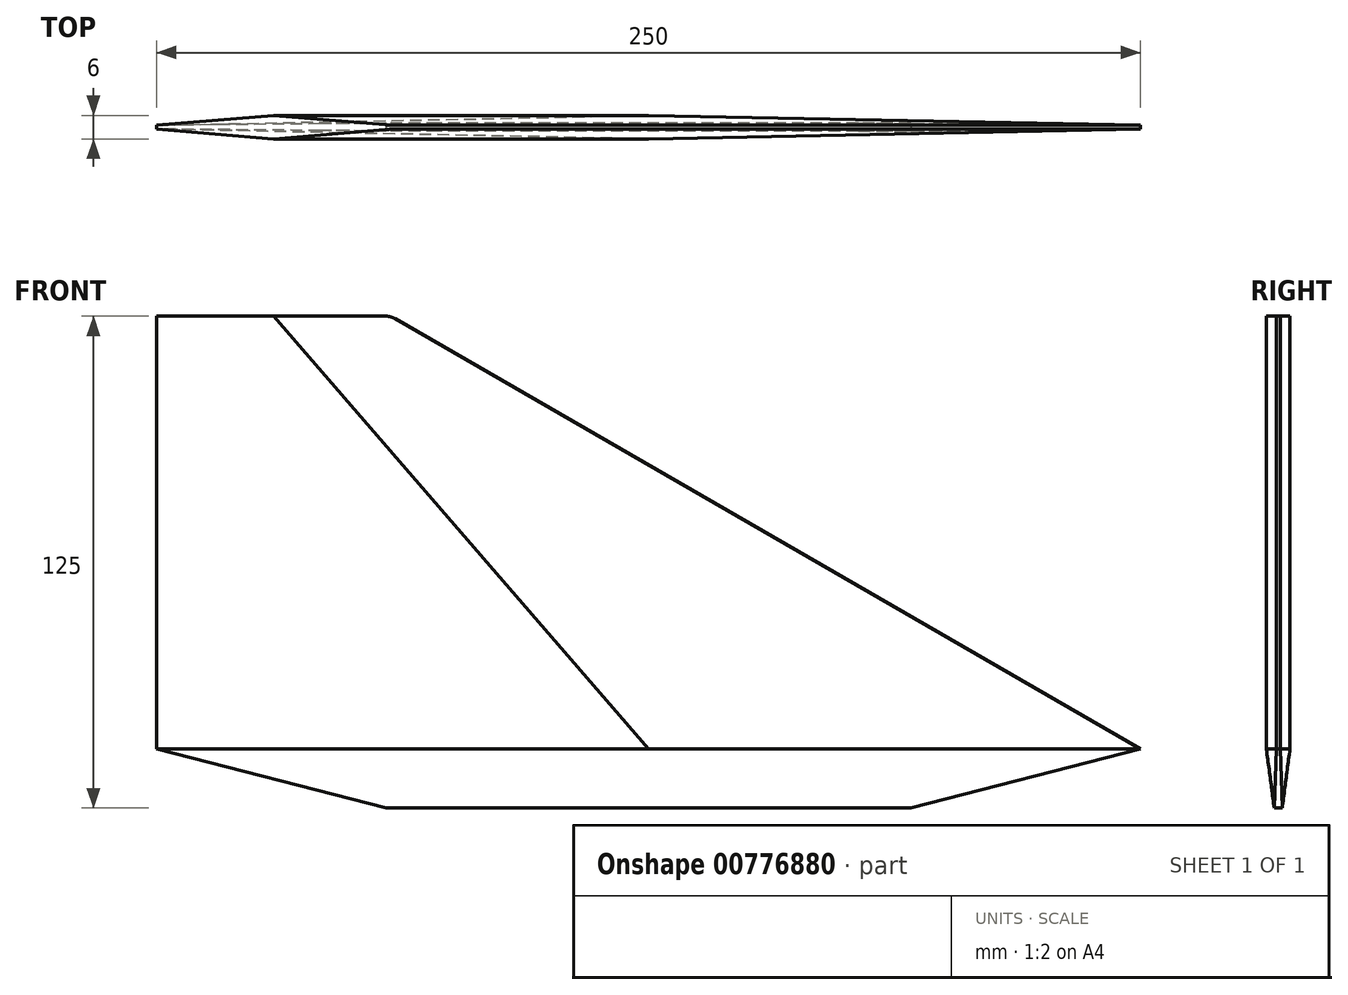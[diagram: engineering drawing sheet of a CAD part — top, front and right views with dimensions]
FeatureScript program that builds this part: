
annotation { "Feature Type Name" : "Feature", "Feature Type Description" : "" }
export const myFeature = defineFeature(function(context is Context, id is Id, definition is map)
    precondition{}
    {
        {
            var Q0;
            Q0=qCreatedBy(makeId("Top.planeOp"),FACE);
            cPlane(context, id + "F0", {"entities" : qUnion([Q0]), "cplaneType" : CPlaneType.OFFSET, "offset" : 15 * mm, "width" : 152.4 * mm, "height" : 152.4 * mm});
        }
        {
            var Q0;
            Q0=qCreatedBy(id+"F0.planeOp",FACE);
            cPlane(context, id + "F1", {"entities" : qUnion([Q0]), "cplaneType" : CPlaneType.OFFSET, "offset" : 110 * mm, "width" : 150 * mm, "height" : 150 * mm});
        }
        {
            var Q0;
            Q0=qCreatedBy(id+"F0.planeOp",FACE);
            var sketch = newSketch(context, id + "F2", { "sketchPlane" : qUnion([Q0])});
            skLineSegment(sketch, "E0", {"start": v(0, -3) * mm, "end": v(0, 0) * mm, "construction": true});
            skLineSegment(sketch, "E1", {"start": v(0, 0) * mm, "end": v(0, 3) * mm, "construction": true});
            skLineSegment(sketch, "E2", {"start": v(0, -3) * mm, "end": v(125, -0.5) * mm});
            skLineSegment(sketch, "E3", {"start": v(125, -0.5) * mm, "end": v(125, 0.5) * mm});
            skLineSegment(sketch, "E4", {"start": v(125, 0.5) * mm, "end": v(0, 3) * mm});
            skLineSegment(sketch, "E5.MirrorCS", {"start": v(-125, -0.5) * mm, "end": v(-125, 0.5) * mm});
            skLineSegment(sketch, "E6.MirrorCS", {"start": v(0, -3) * mm, "end": v(-125, -0.5) * mm});
            skLineSegment(sketch, "E7.MirrorCS", {"start": v(-125, 0.5) * mm, "end": v(0, 3) * mm});
            skSolve(sketch);
        }
        {
            var Q0;
            Q0=qCreatedBy(id+"F1.planeOp",FACE);
            var sketch = newSketch(context, id + "F3", { "sketchPlane" : qUnion([Q0])});
            skLineSegment(sketch, "E8", {"start": v(-95.26, -3) * mm, "end": v(-95.26, 0) * mm, "construction": true});
            skLineSegment(sketch, "E9", {"start": v(-95.26, 0) * mm, "end": v(-95.26, 3) * mm, "construction": true});
            skLineSegment(sketch, "E10", {"start": v(-95.26, -3) * mm, "end": v(-65.53, -0.5) * mm});
            skLineSegment(sketch, "E11", {"start": v(-65.53, -0.5) * mm, "end": v(-65.53, 0.5) * mm});
            skLineSegment(sketch, "E12", {"start": v(-65.53, 0.5) * mm, "end": v(-95.26, 3) * mm});
            skLineSegment(sketch, "E13.MirrorCS", {"start": v(-125, -0.5) * mm, "end": v(-125, 0.5) * mm});
            skLineSegment(sketch, "E14.MirrorCS", {"start": v(-95.26, -3) * mm, "end": v(-125, -0.5) * mm});
            skLineSegment(sketch, "E15.MirrorCS", {"start": v(-125, 0.5) * mm, "end": v(-95.26, 3) * mm});
            skSolve(sketch);
        }
        {
            var Q0;
            Q0=qCreatedBy(makeId("Top.planeOp"),FACE);
            var sketch = newSketch(context, id + "F4", { "sketchPlane" : qUnion([Q0])});
            skLineSegment(sketch, "E16.left", {"start": v(-66.67, 1) * mm, "end": v(-66.67, -1) * mm});
            skLineSegment(sketch, "E16.right", {"start": v(66.67, 1) * mm, "end": v(66.67, -1) * mm});
            skPoint(sketch, "E16.middle", {"position": v(0, 0) * mm});
            skLineSegment(sketch, "E17", {"start": v(66.67, 1) * mm, "end": v(0, 1) * mm});
            skLineSegment(sketch, "E18", {"start": v(0, 1) * mm, "end": v(-66.67, 1) * mm});
            skLineSegment(sketch, "E19", {"start": v(66.67, -1) * mm, "end": v(0, -1) * mm});
            skLineSegment(sketch, "E20", {"start": v(0, -1) * mm, "end": v(-66.67, -1) * mm});
            skSolve(sketch);
        }
        {
            var Q0;
            Q0=qSketchRegion(id+"F4",true);
            var Q1;
            Q1=qSketchRegion(id+"F2",true);
            loft(context, id + "F5", {"sheetProfilesArray" : [{ "sheetProfileEntities" : qUnion([Q0]) }, { "sheetProfileEntities" : qUnion([Q1]) }]});
        }
        {
            var Q1;
            Q1=qSketchRegion(id+"F3",true);
            var Q2;
            Q2=qSketchRegion(id+"F2",true);
            loft(context, id + "F6", {"operationType" : NewBodyOperationType.ADD, "sheetProfilesArray" : [{ "sheetProfileEntities" : qUnion([Q1]) }, { "sheetProfileEntities" : qUnion([Q2]) }]});
        }
        {
            var Q0;
            Q0=qCreatedBy(makeId("Right.planeOp"),FACE);
            cPlane(context, id + "F7", {"entities" : qUnion([Q0]), "cplaneType" : CPlaneType.OFFSET, "offset" : 115 * mm, "oppositeDirection" : true, "width" : 150 * mm, "height" : 150 * mm});
        }
        {
            var Q0;
            Q0=qCreatedBy(makeId("Right.planeOp"),FACE);
            cPlane(context, id + "F8", {"entities" : qUnion([Q0]), "cplaneType" : CPlaneType.OFFSET, "offset" : 125 * mm, "width" : 150 * mm, "height" : 150 * mm});
        }
        {
            var Q0;
            Q0=qCreatedBy(id+"F7.planeOp",FACE);
            var sketch = newSketch(context, id + "F9", { "sketchPlane" : qUnion([Q0])});
            skLineSegment(sketch, "E21", {"start": v(0, 0) * mm, "end": v(0, -93.63) * mm, "construction": true});
            skArc(sketch, "E22", {"start": v(45.5, -22.12) * mm, "mid": v(0, -7) * mm, "end": v(-45.5, -22.12) * mm, "construction": true});
            skArc(sketch, "E23", {"start": v(20, -9.68) * mm, "mid": v(0, -7) * mm, "end": v(-20, -9.68) * mm});
            skLineSegment(sketch, "E24", {"start": v(0.5, 15) * mm, "end": v(-0.5, 15) * mm});
            skArc(sketch, "E25", {"start": v(0.5, 15) * mm, "mid": v(9.76, 2.28) * mm, "end": v(20, -9.68) * mm});
            skArc(sketch, "E26", {"start": v(-20, -9.68) * mm, "mid": v(-9.76, 2.28) * mm, "end": v(-0.5, 15) * mm});
            skSolve(sketch);
        }
        {
            var Q0;
            Q0=qCreatedBy(makeId("Right.planeOp"),FACE);
            var sketch = newSketch(context, id + "F10", { "sketchPlane" : qUnion([Q0])});
            skLineSegment(sketch, "E27", {"start": v(0, -1.91) * mm, "end": v(0, -93.63) * mm, "construction": true});
            skArc(sketch, "E28", {"start": v(45.5, -22.12) * mm, "mid": v(0, -7) * mm, "end": v(-45.5, -22.12) * mm, "construction": true});
            skArc(sketch, "E29", {"start": v(20, -9.68) * mm, "mid": v(0, -7) * mm, "end": v(-20, -9.68) * mm});
            skArc(sketch, "E30", {"start": v(3, 15) * mm, "mid": v(10.33, 1.86) * mm, "end": v(20, -9.68) * mm});
            skArc(sketch, "E31.MirrorCS", {"start": v(-3, 15) * mm, "mid": v(-10.33, 1.86) * mm, "end": v(-20, -9.68) * mm});
            skLineSegment(sketch, "E32", {"start": v(3, 15) * mm, "end": v(-3, 15) * mm});
            skSolve(sketch);
        }
        {
            var Q0;
            Q0=qCreatedBy(id+"F0.planeOp",FACE);
            var Q1;
            Q1=sQuery(id+"F4.wireOp",EDGE,"E18");
            cPlane(context, id + "F11", {"entities" : qUnion([Q0, Q1]), "cplaneType" : CPlaneType.LINE_ANGLE, "offset" : 25 * mm, "angle" : 15 * degree, "width" : 150 * mm, "height" : 150 * mm});
        }
        {
            var Q0;
            Q0=qCreatedBy(id+"F11.planeOp",FACE);
            cPlane(context, id + "F12", {"entities" : qUnion([Q0]), "cplaneType" : CPlaneType.OFFSET, "offset" : 25 * mm, "oppositeDirection" : true, "width" : 150 * mm, "height" : 150 * mm});
        }
        {
            var Q0;
            Q0=qCreatedBy(id+"F12.planeOp",FACE);
            var sketch = newSketch(context, id + "F13", { "sketchPlane" : qUnion([Q0])});
            skCircle(sketch, "E33", {"center": v(-79.78, -8.83) * mm, "radius": 4.48 * mm});
            skCircle(sketch, "E34.1.0.0", {"center": v(-34.78, -8.83) * mm, "radius": 4.48 * mm});
            skCircle(sketch, "E34.2.0.0", {"center": v(10.22, -8.83) * mm, "radius": 4.48 * mm});
            skLineSegment(sketch, "E34.direction1", {"start": v(-79.78, -8.83) * mm, "end": v(-34.78, -8.83) * mm, "construction": true});
            skSolve(sketch);
        }
        {
            var Q0;
            Q0=qCreatedBy(id+"F12.planeOp",FACE);
            var sketch = newSketch(context, id + "F14", { "sketchPlane" : qUnion([Q0])});
            skCircle(sketch, "E35", {"center": v(-79.78, -8.83) * mm, "radius": 2 * mm});
            skCircle(sketch, "E36.1.0.0", {"center": v(-34.78, -8.83) * mm, "radius": 2 * mm});
            skCircle(sketch, "E36.2.0.0", {"center": v(10.22, -8.83) * mm, "radius": 2 * mm});
            skLineSegment(sketch, "E36.direction1", {"start": v(-79.78, -8.83) * mm, "end": v(-34.78, -8.83) * mm, "construction": true});
            skSolve(sketch);
        }
        {
            var Q0;
            Q0=qSketchRegion(id+"F14",true);
            extrude(context, id + "F15", {"entities" : qUnion([Q0]), "operationType" : NewBodyOperationType.REMOVE, "endBound" : BoundingType.THROUGH_ALL, "depth" : 25 * mm, "offsetDistance" : 25 * mm});
        }
        {
            var Q0;
            Q0=qSketchRegion(id+"F13",true);
            extrude(context, id + "F16", {"entities" : qUnion([Q0]), "operationType" : NewBodyOperationType.REMOVE, "depth" : 26 * mm, "offsetDistance" : 25 * mm});
        }
        {
            var Q0;
            Q0=qCreatedBy(id+"F7.planeOp",FACE);
            cPlane(context, id + "F17", {"entities" : qUnion([Q0]), "cplaneType" : CPlaneType.OFFSET, "offset" : 10 * mm, "oppositeDirection" : true, "width" : 150 * mm, "height" : 150 * mm});
        }
        {
            var Q0;
            Q0=qCreatedBy(id+"F17.planeOp",FACE);
            var sketch = newSketch(context, id + "F18", { "sketchPlane" : qUnion([Q0])});
            skLineSegment(sketch, "E37", {"start": v(0, -2.27) * mm, "end": v(0, -93.99) * mm, "construction": true});
            skArc(sketch, "E38", {"start": v(45.5, -22.12) * mm, "mid": v(0, -7) * mm, "end": v(-45.5, -22.12) * mm, "construction": true});
            skArc(sketch, "E39", {"start": v(2.5, -7.04) * mm, "mid": v(0, -7) * mm, "end": v(-2.5, -7.04) * mm});
            skArc(sketch, "E40", {"start": v(0.5, 15) * mm, "mid": v(0.89, 3.92) * mm, "end": v(2.5, -7.04) * mm});
            skArc(sketch, "E41.MirrorCS", {"start": v(-0.5, 15) * mm, "mid": v(-0.89, 3.92) * mm, "end": v(-2.5, -7.04) * mm});
            skLineSegment(sketch, "E42", {"start": v(0.5, 15) * mm, "end": v(-0.5, 15) * mm});
            skSolve(sketch);
        }
        {
            var Q0;
            Q0=makeQuery(id+"F6.opLoft","MID_CAP_EDGE",EDGE,{"disambiguationData":[OSD([sQuery(id+"F3.wireOp",EDGE,"E10"),sQuery(id+"F3.wireOp",EDGE,"E11"),sQuery(id+"F3.wireOp",EDGE,"E12")])],"capPos":0.0});
            fillet(context, id + "F19", {"entities" : qUnion([Q0]), "radius" : 5 * mm, "tangentPropagation" : true, "allowEdgeOverflow" : false});
        }
    });
